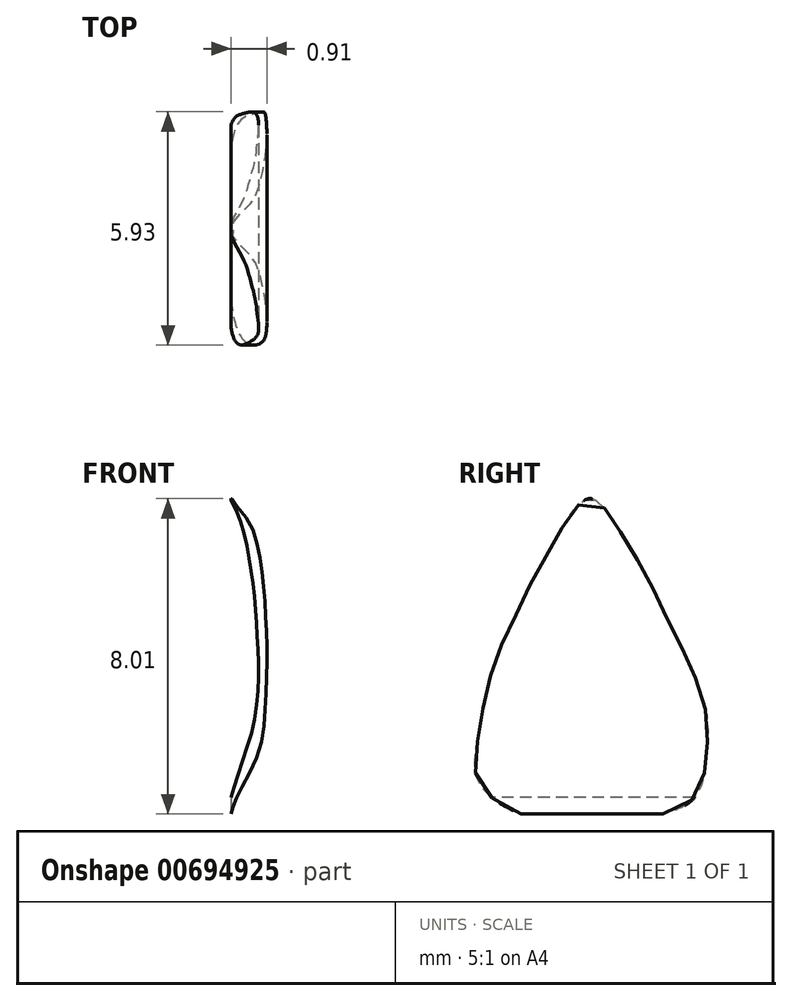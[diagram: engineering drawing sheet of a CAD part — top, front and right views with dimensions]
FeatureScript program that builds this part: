
annotation { "Feature Type Name" : "Feature", "Feature Type Description" : "" }
export const myFeature = defineFeature(function(context is Context, id is Id, definition is map)
    precondition{}
    {
        {
            var Q0;
            Q0=qCreatedBy(makeId("Right.planeOp"),FACE);
            var sketch = newSketch(context, id + "F0", { "sketchPlane" : qUnion([Q0])});
            skPoint(sketch, "E0", {"position": v(0, 0) * mm});
            skFitSpline(sketch, "E1", {"points": [v(0, 5.23) * mm, v(0.74, 4.49) * mm, v(1.52, 3.16) * mm, v(2.08, 2) * mm, v(2.94, 0) * mm, v(2.98, -1.36) * mm, v(2.54, -2.5) * mm, v(0, -2.97) * mm, v(-1.36, -2.9) * mm, v(-2.74, -2.08) * mm, v(-2.84, -1.02) * mm, v(-2.44, 0.9) * mm, v(-1.92, 2.12) * mm, v(-1.48, 3.06) * mm, v(-0.9, 4.09) * mm, v(0, 5.23) * mm]});
            skSolve(sketch);
        }
        {
            var Q0;
            Q0=makeQuery(id+"F0.imprint","IMPRINT",FACE,{"disambiguationData":[TD([[makeQuery(id+"F0.imprint","IMPRINT",EDGE,{"derivedFrom":sQuery(id+"F0.wireOp",EDGE,"E1")}),-1.0]])]});
            extrude(context, id + "F1", {"entities" : qUnion([Q0]), "oppositeDirection" : true, "depth" : 1 * mm, "offsetDistance" : 25 * mm});
        }
        {
            var Q0;
            Q0=qCreatedBy(makeId("Front.planeOp"),FACE);
            var sketch = newSketch(context, id + "F2", { "sketchPlane" : qUnion([Q0])});
            skFitSpline(sketch, "E2", {"points": [v(-0.98, 5.37) * mm, v(-0.62, 4.76) * mm, v(-0.3, 3.94) * mm, v(-0.18, 3.06) * mm, v(-0.1, 1.5) * mm, v(-0.14, -0.26) * mm, v(-0.4, -1.51) * mm, v(-1, -2.95) * mm, v(-0.33, -3.6) * mm, v(0.9, -3.34) * mm, v(1.16, 3.8) * mm, v(0.43, 5.6) * mm, v(-0.98, 5.37) * mm]});
            skFitSpline(sketch, "E3", {"points": [v(-1, 5.18) * mm, v(-0.82, 4.82) * mm, v(-0.7, 4.48) * mm, v(-0.43, 2.92) * mm, v(-0.32, 1.54) * mm, v(-0.44, -0.56) * mm, v(-1.05, -2.76) * mm, v(-1.02, -3.2) * mm, v(-2.21, -3.58) * mm, v(-1.44, 5.23) * mm, v(-1, 5.18) * mm]});
            skSolve(sketch);
        }
        {
            var Q0;
            Q0 = qSketchRegion(id + "F2", true);
            extrude(context, id + "F3", {"entities" : qUnion([Q0]), "operationType" : NewBodyOperationType.REMOVE, "oppositeDirection" : true, "depth" : 8 * mm, "offsetDistance" : 25 * mm, "symmetric" : true});
        }
        {
            var Q0;
            Q0=makeQuery(id+"F1.opExtrude","SWEPT_BODY",BODY,{"disambiguationData":[OSD([sQuery(id+"F0.wireOp",EDGE,"E1")])]});
            transform(context, id + "F4", {"entities" : qUnion([Q0]), "transformType" : TransformType.TRANSLATION_3D, "dx" : 0 * mm, "dy" : 0 * mm, "dz" : 0 * mm, "makeCopy" : true});
        }
    });
